# Revit family: Bath-Whirlpool-Kohler-Sunward-K_1162-Sxx
name_source: partatom
category: Plumbing Fixtures
revit_build: Autodesk Revit Architecture 2014 (Build: 20131024_2115(x64)
units: mm (PartAtom-declared; Revit-internal decimal feet)

## types (9) — shared parameters
ADA Compliant = No
Apparent Load = 120 VA
Assembly Code = D2010510
CW Connection = No
Default Elevation = 0' - 0"
Drain Diameter = 0' - 1 1/2"
Electrical Note = Provide one grounded electrical outlet within 24'' (610 mm) of each component
HW Connection = No
Height = 1' - 8"
Keynote = 22 40 00.D4
Length = 5' - 0"
Manufacturer = Kohler
Material = ExoCrylic
Number of Poles = 1
Product Documentation Link = http://www.us.kohler.com
Product Name = Sunward 60'' x 42'' Drop-In Whirpool
Product Page URL = http://www.us.kohler.com
Sanitary Connector = Sanitary Drain
URL = http://www.us.kohler.com
Vent Connection = Yes
Version = 2014 - v1.0a
Voltage = 120 V
Waste Connection = Yes
Water Capacity = 57 gal (215.8 L)
Width = 3' - 6"
zero-valued in all types: CWFU, HWFU, Power Factor, WFU

## per-type parameters (varying)
| type | Constraint | ControlM | Description | Electrical Connector | Finish | Model | Weight |
| 0-White | 1 | 0 | 60'' X 42'' Drop-in Whirlpool, White | One Connector, Pump Only: 120 V, 7.5 A, 60 Hz | Acrylic - Kohler - 0 - White | K-1162-S1-0 | 110 lbs (49.9 kg) |
| 47-Almond | 1 | 47 | 60'' X 42'' Drop-in Whirlpool, Almond | One Connector, Pump Only: 120 V, 7.5 A, 60 Hz | Acrylic - Kohler - 47 - Almond | K-1162-S1-47 | 110 lbs (49.9 kg) |
| 96-Biscuit | 1 | 96 | 60'' X 42'' Drop-in Whirlpool, Biscuit | One Connector, Pump Only: 120 V, 7.5 A, 60 Hz | Acrylic - Kohler - 96 - Biscuit | K-1162-S1-96 | 110 lbs (49.9 kg) |
| Heater, 0-White | 2 | 0 | 60'' X 42'' Drop-in Whirlpool with Heater, White | Two Connectors, Pump and Heater: 120 V, 7.5 A, 60 Hz | Acrylic - Kohler - 0 - White | K-1162-S1H-0 | 110 lbs (49.9 kg) |
| Heater, 47-Almond | 2 | 47 | 60'' X 42'' Drop-in Whirlpool with Heater, Almond | Two Connectors, Pump and Heater: 120 V, 7.5 A, 60 Hz | Acrylic - Kohler - 47 - Almond | K-1162-S1H-47 | 110 lbs (49.9 kg) |
| Heater, 96-Biscuit | 2 | 96 | 60'' X 42'' Drop-in Whirlpool with Heater, Biscuit | Two Connectors, Pump and Heater: 120 V, 7.5 A, 60 Hz | Acrylic - Kohler - 96 - Biscuit | K-1162-S1H-96 | 110 lbs (49.9 kg) |
| Bask Heated Surface, 0-White | 3 | 0 | 60'' X 42'' Drop-in Whirlpool with Bask Heated Surface, White | One Connector, Pump and Heated Surface: 120 V, 7.5 A, 60 Hz | Acrylic - Kohler - 0 - White | K-1162-S1W-0 | 116 lbs (52.6 kg) |
| Bask Heated Surface, 47-Almond | 3 | 47 | 60'' X 42'' Drop-in Whirlpool with Bask Heated Surface, Almond | One Connector, Pump and Heated Surface: 120 V, 7.5 A, 60 Hz | Acrylic - Kohler - 47 - Almond | K-1162-S1W-47 | 116 lbs (52.6 kg) |
| Bask Heated Surface, 96-Biscuit | 3 | 96 | 60'' X 42'' Drop-in Whirlpool with Bask Heated Surface, Biscuit | One Connector, Pump and Heated Surface: 120 V, 7.5 A, 60 Hz | Acrylic - Kohler - 96 - Biscuit | K-1162-S1W-96 | 116 lbs (52.6 kg) |

## geometry (parser evidence)
native form markers: Extrusion x3, Sweep x1
no freeform markers — native parametric forms only
